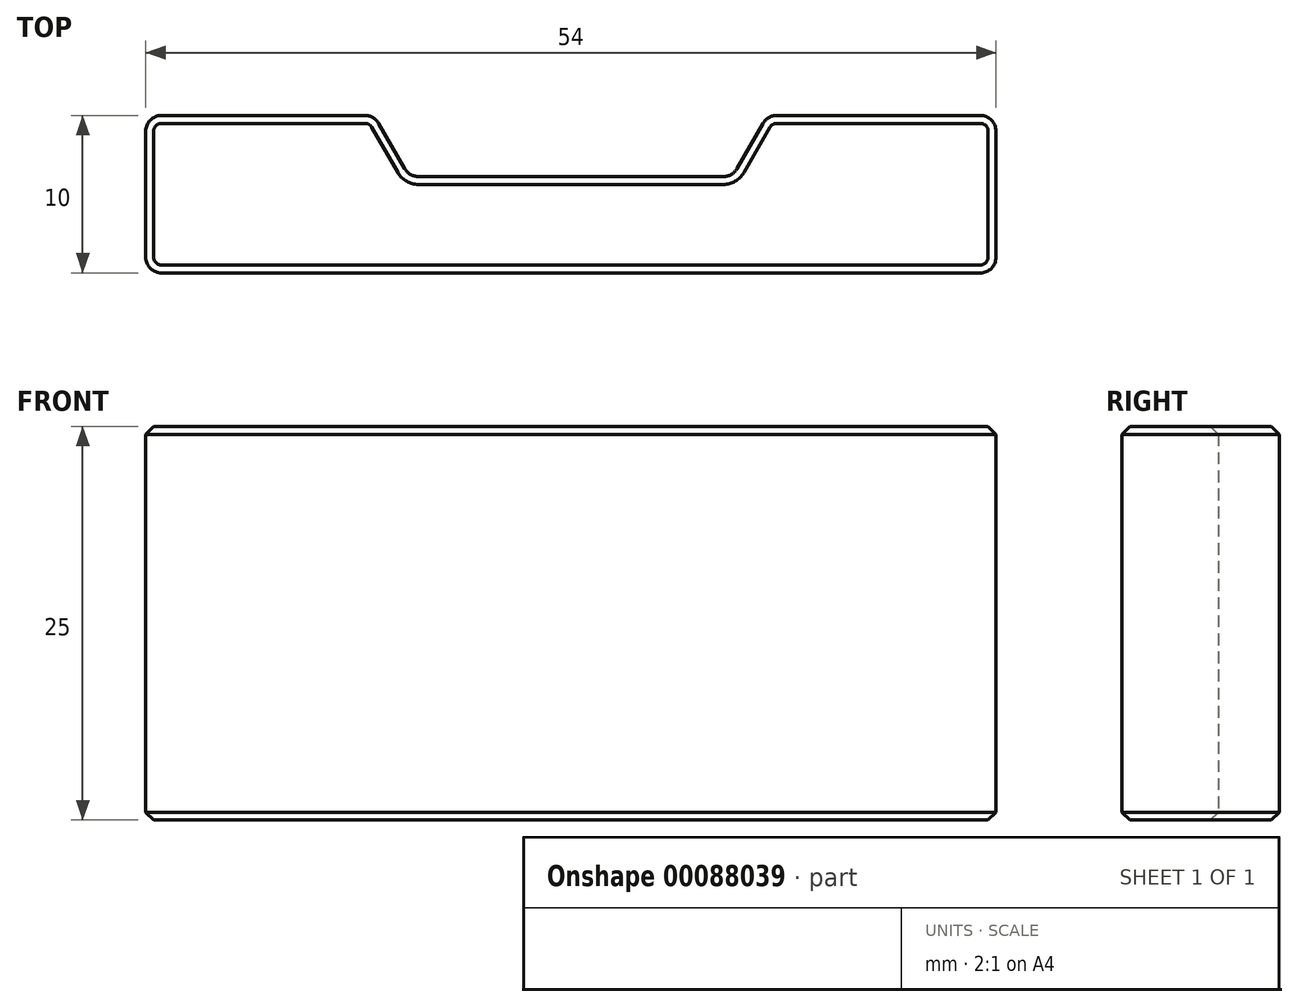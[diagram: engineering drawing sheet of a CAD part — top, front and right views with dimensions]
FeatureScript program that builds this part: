
annotation { "Feature Type Name" : "Feature", "Feature Type Description" : "" }
export const myFeature = defineFeature(function(context is Context, id is Id, definition is map)
    precondition{}
    {
        {
            var Q0;
            Q0=qCreatedBy(makeId("Top.planeOp"),FACE);
            var sketch = newSketch(context, id + "F0", { "sketchPlane" : qUnion([Q0])});
            skLineSegment(sketch, "E0", {"start": v(0, 0) * mm, "end": v(-26, 0) * mm});
            skLineSegment(sketch, "E1", {"start": v(-27, 1) * mm, "end": v(-27, 9) * mm});
            skLineSegment(sketch, "E2", {"start": v(-26, 10) * mm, "end": v(-13.08, 10) * mm});
            skLineSegment(sketch, "E3", {"start": v(-12.21, 9.5) * mm, "end": v(-10.55, 6.62) * mm});
            skLineSegment(sketch, "E4", {"start": v(-9.68, 6.12) * mm, "end": v(0, 6.12) * mm});
            skLineSegment(sketch, "E5", {"start": v(0, 6.12) * mm, "end": v(0, 0) * mm, "construction": true});
            skLineSegment(sketch, "E6.MirrorCS", {"start": v(9.68, 6.12) * mm, "end": v(0, 6.12) * mm});
            skLineSegment(sketch, "E7.MirrorCS", {"start": v(0, 0) * mm, "end": v(26, 0) * mm});
            skLineSegment(sketch, "E8.MirrorCS", {"start": v(12.21, 9.5) * mm, "end": v(10.55, 6.62) * mm});
            skLineSegment(sketch, "E9.MirrorCS", {"start": v(26, 10) * mm, "end": v(13.08, 10) * mm});
            skLineSegment(sketch, "E10.MirrorCS", {"start": v(27, 1) * mm, "end": v(27, 9) * mm});
            skPoint(sketch, "E11.visualSharp", {"position": v(-27, 10) * mm});
            skArc(sketch, "E11.filletArc", {"start": v(-26, 10) * mm, "mid": v(-26.7, 9.7) * mm, "end": v(-27, 9) * mm});
            skPoint(sketch, "E12.visualSharp", {"position": v(-27, 0) * mm});
            skArc(sketch, "E12.filletArc", {"start": v(-27, 1) * mm, "mid": v(-26.7, 0.3) * mm, "end": v(-26, 0) * mm});
            skPoint(sketch, "E13.visualSharp", {"position": v(27, 0) * mm});
            skArc(sketch, "E13.filletArc", {"start": v(26, 0) * mm, "mid": v(26.7, 0.3) * mm, "end": v(27, 1) * mm});
            skPoint(sketch, "E14.visualSharp", {"position": v(27, 10) * mm});
            skArc(sketch, "E14.filletArc", {"start": v(27, 9) * mm, "mid": v(26.7, 9.7) * mm, "end": v(26, 10) * mm});
            skPoint(sketch, "E15.visualSharp", {"position": v(-12.5, 10) * mm});
            skArc(sketch, "E15.filletArc", {"start": v(-12.21, 9.5) * mm, "mid": v(-12.58, 9.87) * mm, "end": v(-13.08, 10) * mm});
            skPoint(sketch, "E16.visualSharp", {"position": v(-10.26, 6.12) * mm});
            skArc(sketch, "E16.filletArc", {"start": v(-10.55, 6.62) * mm, "mid": v(-10.18, 6.25) * mm, "end": v(-9.68, 6.12) * mm});
            skPoint(sketch, "E17.visualSharp", {"position": v(10.26, 6.12) * mm});
            skArc(sketch, "E17.filletArc", {"start": v(9.68, 6.12) * mm, "mid": v(10.18, 6.25) * mm, "end": v(10.55, 6.62) * mm});
            skPoint(sketch, "E18.visualSharp", {"position": v(12.5, 10) * mm});
            skArc(sketch, "E18.filletArc", {"start": v(13.08, 10) * mm, "mid": v(12.58, 9.87) * mm, "end": v(12.21, 9.5) * mm});
            skSolve(sketch);
        }
        {
            var Q0;
            Q0=makeQuery(id+"F0.imprint","IMPRINT",FACE,{"disambiguationData":[TD([[makeQuery(id+"F0.imprint","IMPRINT",EDGE,{"derivedFrom":sQuery(id+"F0.wireOp",EDGE,"E0")}),-1.0]])]});
            extrude(context, id + "F1", {"entities" : qUnion([Q0]), "depth" : 25 * mm});
        }
        {
            var Q0;
            Q0=makeQuery(id+"F1.opExtrude","CAP_EDGE",EDGE,{"disambiguationData":[OSD([sQuery(id+"F0.wireOp",EDGE,"E9.MirrorCS")])],"isStart":false});
            var Q1;
            Q1=makeQuery(id+"F1.opExtrude","CAP_EDGE",EDGE,{"disambiguationData":[OSD([sQuery(id+"F0.wireOp",EDGE,"E2")])],"isStart":true});
            chamfer(context, id + "F2", {"entities" : qUnion([Q0, Q1]), "width" : 0.5 * mm, "tangentPropagation" : true});
        }
    });
